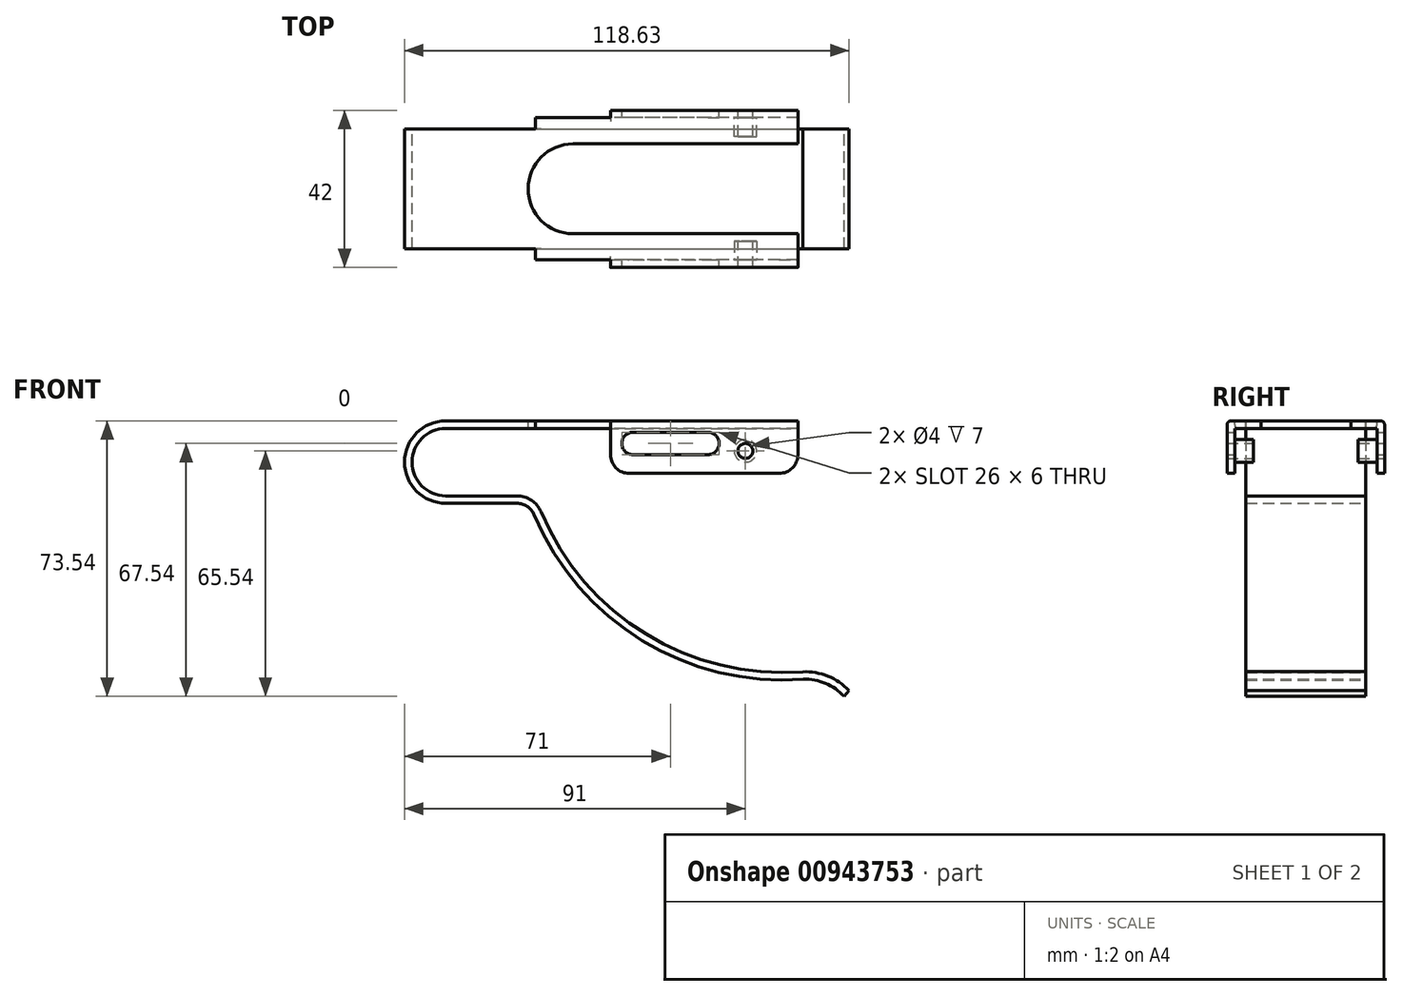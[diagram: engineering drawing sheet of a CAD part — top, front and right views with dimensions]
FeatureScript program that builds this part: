
annotation { "Feature Type Name" : "Feature", "Feature Type Description" : "" }
export const myFeature = defineFeature(function(context is Context, id is Id, definition is map)
    precondition{}
    {
        {
            var Q0;
            Q0=qCreatedBy(makeId("Front.planeOp"),FACE);
            var sketch = newSketch(context, id + "F0", { "sketchPlane" : qUnion([Q0])});
            skArc(sketch, "E0", {"start": v(0, 11) * mm, "mid": v(-11, 0) * mm, "end": v(0, -11) * mm});
            skLineSegment(sketch, "E1", {"start": v(0, 11) * mm, "end": v(94, 11) * mm});
            skLineSegment(sketch, "E2", {"start": v(0, -11) * mm, "end": v(19, -11) * mm});
            skArc(sketch, "E3", {"start": v(23.61, -14.06) * mm, "mid": v(52.42, -47.62) * mm, "end": v(95.41, -58) * mm});
            skArc(sketch, "E4", {"start": v(106.34, -62.54) * mm, "mid": v(101.38, -59.06) * mm, "end": v(95.41, -58) * mm});
            skPoint(sketch, "E5.visualSharp", {"position": v(22.4, -11) * mm});
            skArc(sketch, "E5.filletArc", {"start": v(23.61, -14.06) * mm, "mid": v(21.77, -11.84) * mm, "end": v(19, -11) * mm});
            skArc(sketch, "E6.0", {"start": v(107.63, -61) * mm, "mid": v(102, -57.16) * mm, "end": v(95.3, -56) * mm});
            skArc(sketch, "E6.1", {"start": v(25.45, -13.3) * mm, "mid": v(53.48, -45.92) * mm, "end": v(95.3, -56) * mm});
            skLineSegment(sketch, "E6.2", {"start": v(0, 9) * mm, "end": v(94, 9) * mm});
            skArc(sketch, "E6.3", {"start": v(0, 9) * mm, "mid": v(-9, 0) * mm, "end": v(0, -9) * mm});
            skLineSegment(sketch, "E6.4", {"start": v(0, -9) * mm, "end": v(19, -9) * mm});
            skArc(sketch, "E6.5", {"start": v(25.45, -13.3) * mm, "mid": v(22.88, -10.17) * mm, "end": v(19, -9) * mm});
            skLineSegment(sketch, "E7", {"start": v(94, 11) * mm, "end": v(94, 9) * mm});
            skLineSegment(sketch, "E8", {"start": v(106.34, -62.54) * mm, "end": v(107.63, -61) * mm});
            skSolve(sketch);
        }
        {
            var Q0;
            Q0=qSketchRegion(id+"F0",true);
            extrude(context, id + "F1", {"entities" : qUnion([Q0]), "depth" : 16 * mm, "offsetDistance" : 25 * mm});
        }
        {
            var Q0;
            Q0=makeQuery(id+"F1.opExtrude","SWEPT_FACE",FACE,{"disambiguationData":[OSD([sQuery(id+"F0.wireOp",EDGE,"E1")])]});
            var sketch = newSketch(context, id + "F2", { "sketchPlane" : qUnion([Q0])});
            skLineSegment(sketch, "E9.bottom", {"start": v(94, -16) * mm, "end": v(24, -16) * mm});
            skLineSegment(sketch, "E9.top", {"start": v(94, -19) * mm, "end": v(24, -19) * mm});
            skLineSegment(sketch, "E9.left", {"start": v(94, -16) * mm, "end": v(94, -19) * mm});
            skLineSegment(sketch, "E9.right", {"start": v(24, -16) * mm, "end": v(24, -19) * mm});
            skSolve(sketch);
        }
        {
            var Q0;
            Q0=makeQuery(id+"F2.imprint","IMPRINT",FACE,{"disambiguationData":[TD([[makeQuery(id+"F2.imprint","IMPRINT",EDGE,{"derivedFrom":sQuery(id+"F2.wireOp",EDGE,"E9.bottom")}),-1.0]])]});
            extrude(context, id + "F3", {"entities" : qUnion([Q0]), "operationType" : NewBodyOperationType.ADD, "oppositeDirection" : true, "depth" : 2 * mm, "offsetDistance" : 25 * mm});
        }
        {
            var Q0;
            Q0=makeQuery(id+"F3.opExtrude","SWEPT_FACE",FACE,{"disambiguationData":[OSD([sQuery(id+"F2.wireOp",EDGE,"E9.top")])]});
            var sketch = newSketch(context, id + "F4", { "sketchPlane" : qUnion([Q0])});
            skLineSegment(sketch, "E10.bottom", {"start": v(94, 11) * mm, "end": v(44, 11) * mm});
            skLineSegment(sketch, "E10.top", {"start": v(94, -3) * mm, "end": v(44, -3) * mm});
            skLineSegment(sketch, "E10.left", {"start": v(94, 11) * mm, "end": v(94, -3) * mm});
            skLineSegment(sketch, "E10.right", {"start": v(44, 11) * mm, "end": v(44, -3) * mm});
            skSolve(sketch);
        }
        {
            var Q0;
            Q0=qSketchRegion(id+"F4",true);
            extrude(context, id + "F5", {"entities" : qUnion([Q0]), "operationType" : NewBodyOperationType.ADD, "depth" : 2 * mm, "offsetDistance" : 25 * mm});
        }
        {
            var Q0;
            Q0=makeQuery(id+"F5.opExtrude","CAP_EDGE",EDGE,{"disambiguationData":[OSD([sQuery(id+"F4.wireOp",EDGE,"E10.bottom")])],"isStart":false});
            var Q1;
            {var subQ0=sQuery(id+"F2.wireOp",EDGE,"E9.top");Q1=makeQuery(id+"F5.boolean.opBoolean","SPLIT",EDGE,{"disambiguationData":[topologyDisambiguationEdgeConnected([makeQuery(id+"F5.opExtrude","CAP_FACE",FACE,{"disambiguationData":[OSD([sQuery(id+"F4.wireOp",EDGE,"E10.bottom"),sQuery(id+"F4.wireOp",EDGE,"E10.top"),sQuery(id+"F4.wireOp",EDGE,"E10.left"),sQuery(id+"F4.wireOp",EDGE,"E10.right")])],"isStart":true})])],"derivedFrom":makeQuery(id+"F3.opExtrude","CAP_EDGE",EDGE,{"disambiguationData":[OSD([subQ0])],"isStart":false})});}
            fillet(context, id + "F6", {"entities" : qUnion([Q0, Q1]), "radius" : 1 * mm, "tangentPropagation" : true, "allowEdgeOverflow" : false});
        }
        {
            var Q0;
            Q0=makeQuery(id+"F1.opExtrude","SWEPT_BODY",BODY,{"disambiguationData":[OSD([sQuery(id+"F0.wireOp",EDGE,"E0"),sQuery(id+"F0.wireOp",EDGE,"E1"),sQuery(id+"F0.wireOp",EDGE,"E2"),sQuery(id+"F0.wireOp",EDGE,"E3"),sQuery(id+"F0.wireOp",EDGE,"E4"),sQuery(id+"F0.wireOp",EDGE,"E5.filletArc"),sQuery(id+"F0.wireOp",EDGE,"E6.0"),sQuery(id+"F0.wireOp",EDGE,"E6.1"),sQuery(id+"F0.wireOp",EDGE,"E6.2"),sQuery(id+"F0.wireOp",EDGE,"E6.3"),sQuery(id+"F0.wireOp",EDGE,"E6.4"),sQuery(id+"F0.wireOp",EDGE,"E6.5"),sQuery(id+"F0.wireOp",EDGE,"E7"),sQuery(id+"F0.wireOp",EDGE,"E8")])]});
            var Q1;
            Q1=qCreatedBy(makeId("Front.planeOp"),FACE);
            mirror(context, id + "F7", {"operationType" : NewBodyOperationType.ADD, "entities" : qUnion([Q0]), "mirrorPlane" : qUnion([Q1])});
        }
        {
            var Q0;
            {var subQ0=makeQuery(id+"F5.boolean.opBoolean","MERGE",FACE,{"derivedFrom":[makeQuery(id+"F3.boolean.opBoolean","MERGE",FACE,{"derivedFrom":[makeQuery(id+"F1.opExtrude","SWEPT_FACE",FACE,{"disambiguationData":[OSD([sQuery(id+"F0.wireOp",EDGE,"E1")])]}),makeQuery(id+"F3.opExtrude","CAP_FACE",FACE,{"disambiguationData":[OSD([sQuery(id+"F2.wireOp",EDGE,"E9.bottom"),sQuery(id+"F2.wireOp",EDGE,"E9.top"),sQuery(id+"F2.wireOp",EDGE,"E9.left"),sQuery(id+"F2.wireOp",EDGE,"E9.right")])],"isStart":true})]}),makeQuery(id+"F5.opExtrude","SWEPT_FACE",FACE,{"disambiguationData":[OSD([sQuery(id+"F4.wireOp",EDGE,"E10.bottom")])]})]});Q0=makeQuery(id+"F7.boolean.opBoolean","MERGE",FACE,{"derivedFrom":[subQ0,makeQuery(id+"F7.opPattern","COPY",FACE,{"derivedFrom":subQ0,"instanceName":"1"})]});}
            var sketch = newSketch(context, id + "F8", { "sketchPlane" : qUnion([Q0])});
            skArc(sketch, "E11", {"start": v(34, 12) * mm, "mid": v(22, 0) * mm, "end": v(34, -12) * mm});
            skLineSegment(sketch, "E12", {"start": v(34, 12) * mm, "end": v(94, 12) * mm});
            skLineSegment(sketch, "E13", {"start": v(94, 12) * mm, "end": v(94, -12) * mm});
            skLineSegment(sketch, "E14", {"start": v(94, -12) * mm, "end": v(34, -12) * mm});
            skSolve(sketch);
        }
        {
            var Q0;
            Q0=qSketchRegion(id+"F8",true);
            extrude(context, id + "F9", {"entities" : qUnion([Q0]), "operationType" : NewBodyOperationType.REMOVE, "oppositeDirection" : true, "depth" : 2 * mm, "offsetDistance" : 25 * mm});
        }
        {
            var Q0;
            Q0=makeQuery(id+"F7.opPattern","COPY",FACE,{"derivedFrom":makeQuery(id+"F5.opExtrude","CAP_FACE",FACE,{"disambiguationData":[OSD([sQuery(id+"F4.wireOp",EDGE,"E10.bottom"),sQuery(id+"F4.wireOp",EDGE,"E10.top"),sQuery(id+"F4.wireOp",EDGE,"E10.left"),sQuery(id+"F4.wireOp",EDGE,"E10.right")])],"isStart":false}),"instanceName":"1"});
            var sketch = newSketch(context, id + "F10", { "sketchPlane" : qUnion([Q0])});
            skLineSegment(sketch, "E15", {"start": v(-70, 5) * mm, "end": v(-50, 5) * mm});
            skArc(sketch, "E16.0.startCap", {"start": v(-70, 2) * mm, "mid": v(-73, 5) * mm, "end": v(-70, 8) * mm});
            skArc(sketch, "E16.0.endCap", {"start": v(-50, 8) * mm, "mid": v(-47, 5) * mm, "end": v(-50, 2) * mm});
            skLineSegment(sketch, "E16.0.left", {"start": v(-70, 8) * mm, "end": v(-50, 8) * mm});
            skLineSegment(sketch, "E16.0.right", {"start": v(-70, 2) * mm, "end": v(-50, 2) * mm});
            skSolve(sketch);
        }
        {
            var Q0;
            Q0=qSketchRegion(id+"F10",true);
            extrude(context, id + "F11", {"entities" : qUnion([Q0]), "operationType" : NewBodyOperationType.REMOVE, "endBound" : BoundingType.THROUGH_ALL, "oppositeDirection" : true, "depth" : 25 * mm, "offsetDistance" : 25 * mm});
        }
        {
            var Q0;
            Q0=makeQuery(id+"F7.opPattern","COPY",FACE,{"derivedFrom":makeQuery(id+"F5.opExtrude","CAP_FACE",FACE,{"disambiguationData":[OSD([sQuery(id+"F4.wireOp",EDGE,"E10.bottom"),sQuery(id+"F4.wireOp",EDGE,"E10.top"),sQuery(id+"F4.wireOp",EDGE,"E10.left"),sQuery(id+"F4.wireOp",EDGE,"E10.right")])],"isStart":false}),"instanceName":"1"});
            var sketch = newSketch(context, id + "F12", { "sketchPlane" : qUnion([Q0])});
            skPoint(sketch, "E17", {"position": v(-80, 3) * mm});
            skSolve(sketch);
        }
        {
            var Q0;
            Q0=sQuery(id+"F12.wireOp",VERTEX,"E17");
            var Q1;
            Q1=makeQuery(id+"F1.opExtrude","SWEPT_BODY",BODY,{"disambiguationData":[OSD([sQuery(id+"F0.wireOp",EDGE,"E0"),sQuery(id+"F0.wireOp",EDGE,"E1"),sQuery(id+"F0.wireOp",EDGE,"E2"),sQuery(id+"F0.wireOp",EDGE,"E3"),sQuery(id+"F0.wireOp",EDGE,"E4"),sQuery(id+"F0.wireOp",EDGE,"E5.filletArc"),sQuery(id+"F0.wireOp",EDGE,"E6.0"),sQuery(id+"F0.wireOp",EDGE,"E6.1"),sQuery(id+"F0.wireOp",EDGE,"E6.2"),sQuery(id+"F0.wireOp",EDGE,"E6.3"),sQuery(id+"F0.wireOp",EDGE,"E6.4"),sQuery(id+"F0.wireOp",EDGE,"E6.5"),sQuery(id+"F0.wireOp",EDGE,"E7"),sQuery(id+"F0.wireOp",EDGE,"E8")])]});
            hole(context, id + "F13", {"style" : HoleStyle.SIMPLE, "endStyle" : HoleEndStyle.THROUGH, "holeDiameter" : 4 * mm, "majorDiameter" : 5 * mm, "isTappedThrough" : true, "tappedDepth" : 12 * mm, "tapClearance" : 3, "locations" : qUnion([Q0]), "scope" : qUnion([Q1])});
        }
        {
            var Q0;
            Q0=makeQuery(id+"F7.opPattern","COPY",FACE,{"derivedFrom":makeQuery(id+"F5.opExtrude","CAP_FACE",FACE,{"disambiguationData":[OSD([sQuery(id+"F4.wireOp",EDGE,"E10.bottom"),sQuery(id+"F4.wireOp",EDGE,"E10.top"),sQuery(id+"F4.wireOp",EDGE,"E10.left"),sQuery(id+"F4.wireOp",EDGE,"E10.right")])],"isStart":true}),"instanceName":"1"});
            var sketch = newSketch(context, id + "F14", { "sketchPlane" : qUnion([Q0])});
            skCircle(sketch, "E18.0", {"center": v(80, 3) * mm, "radius": 2 * mm});
            skCircle(sketch, "E19.0", {"center": v(80, 3) * mm, "radius": 3 * mm});
            skSolve(sketch);
        }
        {
            var Q0;
            Q0=makeQuery(id+"F14.imprint","IMPRINT",FACE,{"disambiguationData":[TD([[makeQuery(id+"F14.imprint","IMPRINT",EDGE,{"derivedFrom":sQuery(id+"F14.wireOp",EDGE,"E18.0")}),-1.0]])]});
            extrude(context, id + "F15", {"entities" : qUnion([Q0]), "operationType" : NewBodyOperationType.ADD, "depth" : 5 * mm, "offsetDistance" : 25 * mm});
        }
        {
            var Q0;
            Q0=makeQuery(id+"F1.opExtrude","SWEPT_BODY",BODY,{"disambiguationData":[OSD([sQuery(id+"F0.wireOp",EDGE,"E0"),sQuery(id+"F0.wireOp",EDGE,"E1"),sQuery(id+"F0.wireOp",EDGE,"E2"),sQuery(id+"F0.wireOp",EDGE,"E3"),sQuery(id+"F0.wireOp",EDGE,"E4"),sQuery(id+"F0.wireOp",EDGE,"E5.filletArc"),sQuery(id+"F0.wireOp",EDGE,"E6.0"),sQuery(id+"F0.wireOp",EDGE,"E6.1"),sQuery(id+"F0.wireOp",EDGE,"E6.2"),sQuery(id+"F0.wireOp",EDGE,"E6.3"),sQuery(id+"F0.wireOp",EDGE,"E6.4"),sQuery(id+"F0.wireOp",EDGE,"E6.5"),sQuery(id+"F0.wireOp",EDGE,"E7"),sQuery(id+"F0.wireOp",EDGE,"E8")])]});
            var Q1;
            Q1=qCreatedBy(makeId("Front.planeOp"),FACE);
            mirror(context, id + "F16", {"operationType" : NewBodyOperationType.ADD, "entities" : qUnion([Q0]), "mirrorPlane" : qUnion([Q1])});
        }
        {
            var Q0;
            Q0=makeQuery(id+"F7.opPattern","COPY",EDGE,{"derivedFrom":makeQuery(id+"F5.opExtrude","SWEPT_EDGE",EDGE,{"disambiguationData":[OSD([sQuery(id+"F4.wireOp",EDGE,"E10.top"),sQuery(id+"F4.wireOp",EDGE,"E10.left")])]}),"instanceName":"1"});
            var Q1;
            Q1=makeQuery(id+"F7.opPattern","COPY",EDGE,{"derivedFrom":makeQuery(id+"F5.opExtrude","SWEPT_EDGE",EDGE,{"disambiguationData":[OSD([sQuery(id+"F4.wireOp",EDGE,"E10.top"),sQuery(id+"F4.wireOp",EDGE,"E10.right")])]}),"instanceName":"1"});
            var Q2;
            Q2=makeQuery(id+"F5.opExtrude","SWEPT_EDGE",EDGE,{"disambiguationData":[OSD([sQuery(id+"F4.wireOp",EDGE,"E10.top"),sQuery(id+"F4.wireOp",EDGE,"E10.left")])]});
            var Q3;
            Q3=makeQuery(id+"F5.opExtrude","SWEPT_EDGE",EDGE,{"disambiguationData":[OSD([sQuery(id+"F4.wireOp",EDGE,"E10.top"),sQuery(id+"F4.wireOp",EDGE,"E10.right")])]});
            fillet(context, id + "F17", {"entities" : qUnion([Q0, Q1, Q2, Q3]), "radius" : 5 * mm, "tangentPropagation" : true, "allowEdgeOverflow" : false});
        }
    });
